# Revit family: APL Metro Series Thermal Heart French Door Overlight Open Out Vertical Section
name_source: partatom
category: Detail Items
revit_build: Autodesk Revit LT 2018 (Build: 20170223_1515(x64)
units: mm (PartAtom-declared; Revit-internal decimal feet)

## family parameters
Rotate with component = Yes
Section Shape = Not Defined
Shared = No

## types (4) — shared parameters
Coupling = Yes
Fixed = No
Liner Head = Yes
Liner Sill = No
Overlight = 400 mm  [stored 1.31234 ft]
Sash = Yes

## per-type parameters (varying)
| type | Glazing | Liner Block |
| Double Glazing Groove | Double Glazing 31 mm | Liner |
| Single Glazing Groove | Single Glazing | Liner |
| Double Glazing No Groove | Double Glazing 31 mm | Liner No Groove |
| Single Glazing No Groove | Single Glazing | Liner No Groove |

note: [stored X ft] marks values corroborated as IEEE doubles in the binary element streams (Revit-internal decimal feet)

## geometry (parser evidence)
native form markers: Sweep x14
no freeform markers — native parametric forms only
